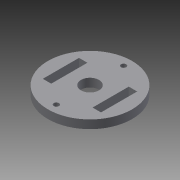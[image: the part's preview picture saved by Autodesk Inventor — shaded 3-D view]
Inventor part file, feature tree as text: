
AUTODESK INVENTOR PART (.ipt)
format: ipt  version: 2013 (Build 170138000, 138)  size: 111,616 bytes
history: native  units: mm
features: other x2, extrude x1, sketch x1
ambient origin geometry x8: Origin, YZ Plane, XZ Plane, XY Plane, X Axis, Y Axis, Z Axis, Center Point
feature tree (4):
  other  "Blocks"
  extrude  "Extrusion3"  Depth=3.0mm
  sketch  "Sketch1"  dims[d0=3.0mm d2=3.0mm d3=0.1mm d7=22.5mm d8=12.4mm d9=4.5mm d10=4.5mm d11=2.0mm d12=2.0mm d23=32.5mm d24=2.0mm d25=12.0mm d28=7.0mm d29=3.25mm d30=14.0mm d31=5.0mm d32=3.25mm d33=0.0mm]
  other  "Block1"
